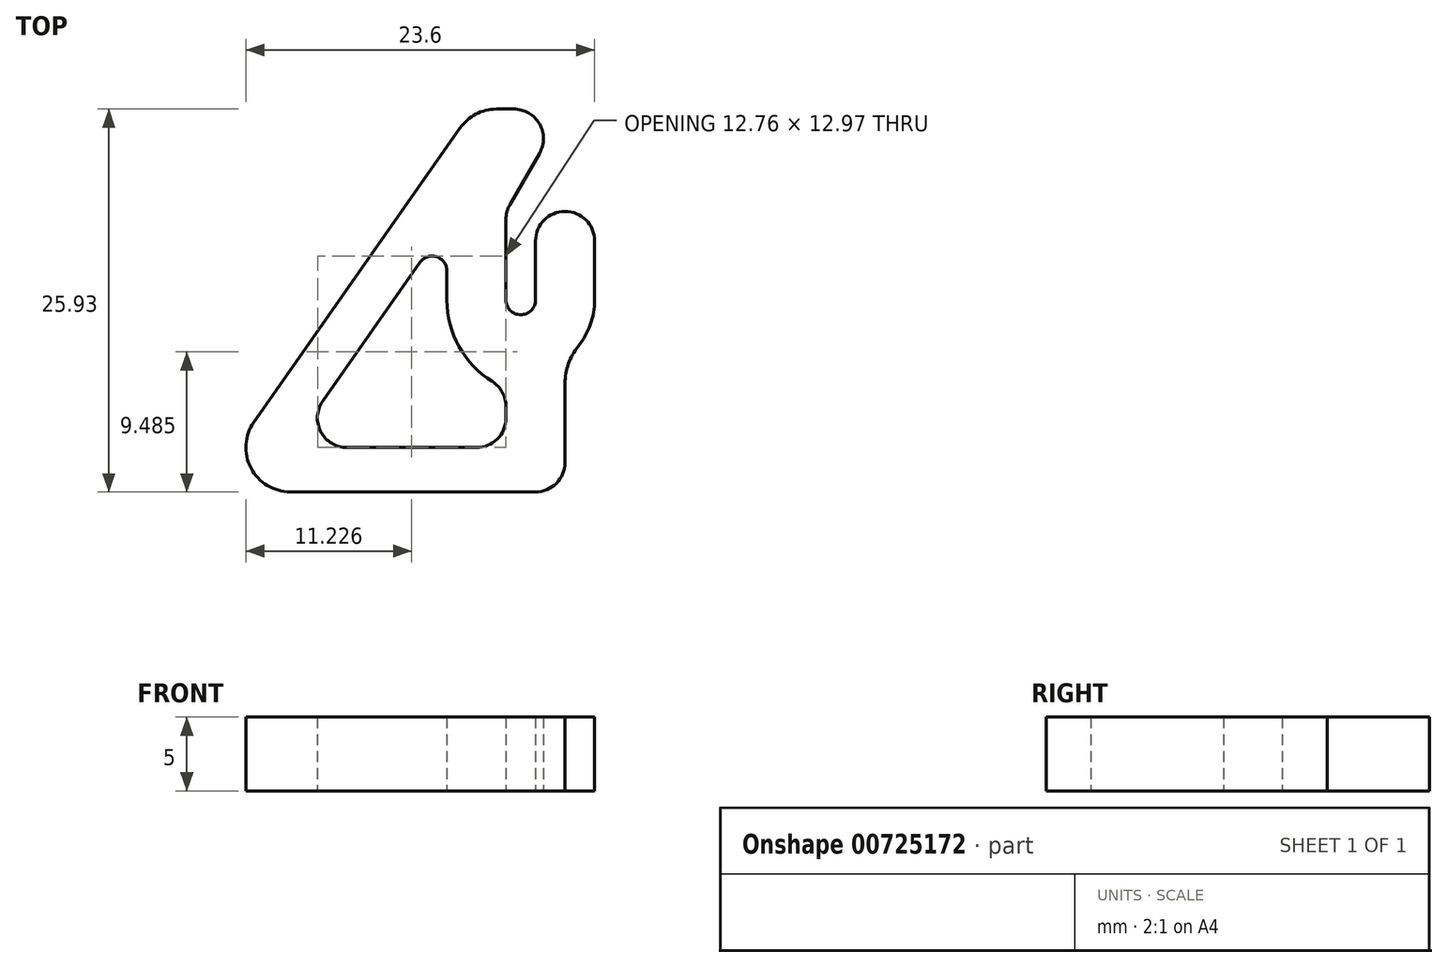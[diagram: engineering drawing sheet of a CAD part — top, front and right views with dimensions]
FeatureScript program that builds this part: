
annotation { "Feature Type Name" : "Feature", "Feature Type Description" : "" }
export const myFeature = defineFeature(function(context is Context, id is Id, definition is map)
    precondition{}
    {
        {
            var Q0;
            Q0=qCreatedBy(makeId("Top.planeOp"),FACE);
            var sketch = newSketch(context, id + "F0", { "sketchPlane" : qUnion([Q0])});
            skLineSegment(sketch, "E0", {"start": v(14.82, 18.93) * mm, "end": v(16, 18.93) * mm});
            skLineSegment(sketch, "E1", {"start": v(17.73, 15.93) * mm, "end": v(15.73, 12.46) * mm});
            skLineSegment(sketch, "E2", {"start": v(15.46, 11.46) * mm, "end": v(15.46, 6) * mm});
            skLineSegment(sketch, "E3", {"start": v(17.46, 6) * mm, "end": v(17.46, 10) * mm});
            skLineSegment(sketch, "E4", {"start": v(21.46, 10) * mm, "end": v(21.46, 6) * mm});
            skArc(sketch, "E5", {"start": v(15.46, 6) * mm, "mid": v(16.46, 5) * mm, "end": v(17.46, 6) * mm});
            skLineSegment(sketch, "E6", {"start": v(-1.6, -2.28) * mm, "end": v(12.36, 17.65) * mm});
            skPoint(sketch, "E7.visualSharp", {"position": v(19.46, 18.93) * mm});
            skArc(sketch, "E7.filletArc", {"start": v(17.73, 15.93) * mm, "mid": v(17.73, 17.93) * mm, "end": v(16, 18.93) * mm});
            skPoint(sketch, "E8.visualSharp", {"position": v(13.25, 18.93) * mm});
            skArc(sketch, "E8.filletArc", {"start": v(14.82, 18.93) * mm, "mid": v(13.43, 18.59) * mm, "end": v(12.36, 17.65) * mm});
            skPoint(sketch, "E9.visualSharp", {"position": v(0, 0) * mm});
            skPoint(sketch, "E10.visualSharp", {"position": v(15.46, 12) * mm});
            skArc(sketch, "E10.filletArc", {"start": v(15.73, 12.46) * mm, "mid": v(15.53, 11.98) * mm, "end": v(15.46, 11.46) * mm});
            skArc(sketch, "E11", {"start": v(21.46, 10) * mm, "mid": v(19.46, 12) * mm, "end": v(17.46, 10) * mm});
            skLineSegment(sketch, "E12", {"start": v(0.86, -7) * mm, "end": v(17.46, -7) * mm});
            skArc(sketch, "E13", {"start": v(20.35, 2.86) * mm, "mid": v(21.18, 4.33) * mm, "end": v(21.46, 6) * mm});
            skPoint(sketch, "E14.visualSharp", {"position": v(-4.9, -7) * mm});
            skArc(sketch, "E14.filletArc", {"start": v(-1.6, -2.28) * mm, "mid": v(-1.8, -5.39) * mm, "end": v(0.86, -7) * mm});
            skLineSegment(sketch, "E15", {"start": v(19.46, -5) * mm, "end": v(19.46, 0.34) * mm});
            skArc(sketch, "E16", {"start": v(20.35, 2.86) * mm, "mid": v(19.7, 1.68) * mm, "end": v(19.46, 0.34) * mm});
            skPoint(sketch, "E17.visualSharp", {"position": v(19.46, -7) * mm});
            skArc(sketch, "E17.filletArc", {"start": v(17.46, -7) * mm, "mid": v(18.88, -6.41) * mm, "end": v(19.46, -5) * mm});
            skLineSegment(sketch, "E18", {"start": v(3.07, -0.85) * mm, "end": v(9.64, 8.54) * mm});
            skLineSegment(sketch, "E19", {"start": v(13.46, -4) * mm, "end": v(4.7, -4) * mm});
            skArc(sketch, "E20.filletArc", {"start": v(3.07, -0.85) * mm, "mid": v(2.93, -2.92) * mm, "end": v(4.7, -4) * mm});
            skLineSegment(sketch, "E21", {"start": v(19.46, 10) * mm, "end": v(19.46, 0.34) * mm, "construction": true});
            skLineSegment(sketch, "E22", {"start": v(15.46, -2) * mm, "end": v(15.46, -1.21) * mm});
            skArc(sketch, "E23", {"start": v(11.46, 6) * mm, "mid": v(12.28, 2.85) * mm, "end": v(14.52, 0.49) * mm});
            skLineSegment(sketch, "E24", {"start": v(11.46, 7.97) * mm, "end": v(11.46, 6) * mm});
            skPoint(sketch, "E25.visualSharp", {"position": v(11.46, 11.14) * mm});
            skArc(sketch, "E25.filletArc", {"start": v(11.46, 7.97) * mm, "mid": v(10.76, 8.92) * mm, "end": v(9.64, 8.54) * mm});
            skPoint(sketch, "E26.visualSharp", {"position": v(15.46, -4) * mm});
            skArc(sketch, "E26.filletArc", {"start": v(13.46, -4) * mm, "mid": v(14.88, -3.41) * mm, "end": v(15.46, -2) * mm});
            skPoint(sketch, "E27.visualSharp", {"position": v(15.46, 0) * mm});
            skArc(sketch, "E27.filletArc", {"start": v(15.46, -1.21) * mm, "mid": v(15.21, -0.24) * mm, "end": v(14.52, 0.49) * mm});
            skLineSegment(sketch, "E28", {"start": v(11.46, 6) * mm, "end": v(15.46, 6) * mm, "construction": true});
            skSolve(sketch);
        }
        {
            var Q0;
            Q0=makeQuery(id+"F0.imprint","IMPRINT",FACE,{"disambiguationData":[TD([[makeQuery(id+"F0.imprint","IMPRINT",EDGE,{"derivedFrom":sQuery(id+"F0.wireOp",EDGE,"E0")}),-1.0]])]});
            extrude(context, id + "F1", {"entities" : qUnion([Q0]), "depth" : 5 * mm, "offsetDistance" : 25 * mm});
        }
    });
